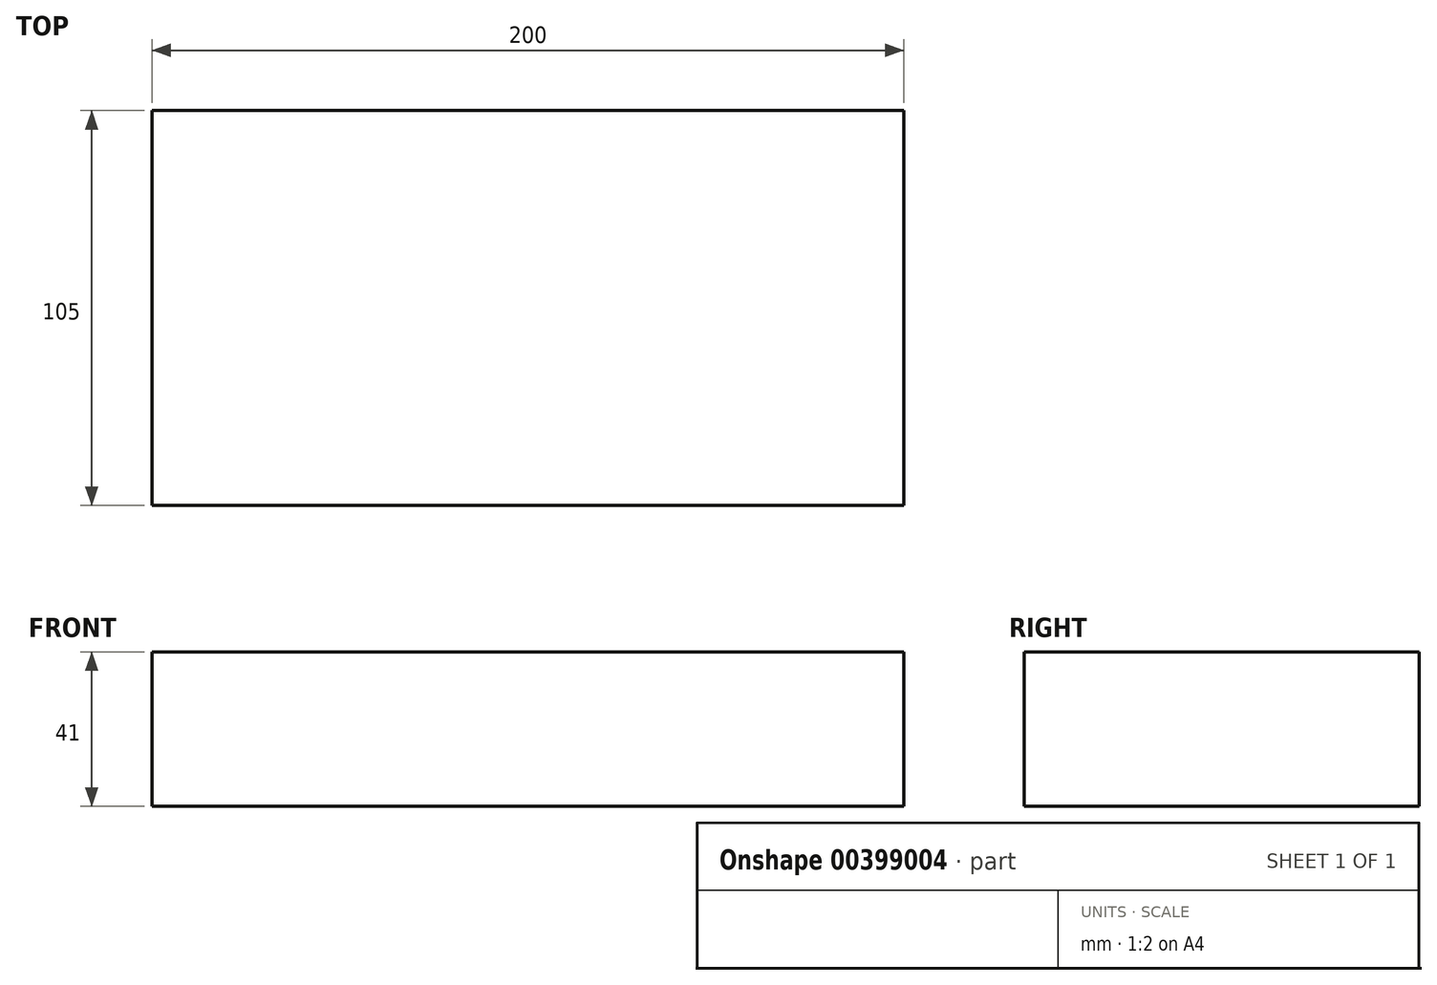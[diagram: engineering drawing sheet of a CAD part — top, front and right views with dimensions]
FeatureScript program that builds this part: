
annotation { "Feature Type Name" : "Feature", "Feature Type Description" : "" }
export const myFeature = defineFeature(function(context is Context, id is Id, definition is map)
    precondition{}
    {
        {
            var Q0;
            Q0=qCreatedBy(makeId("Front.planeOp"),FACE);
            var sketch = newSketch(context, id + "F0", { "sketchPlane" : qUnion([Q0])});
            skLineSegment(sketch, "E0.bottom", {"start": v(0, 0) * mm, "end": v(200, 0) * mm});
            skLineSegment(sketch, "E0.top", {"start": v(0, 41) * mm, "end": v(200, 41) * mm});
            skLineSegment(sketch, "E0.left", {"start": v(0, 0) * mm, "end": v(0, 41) * mm});
            skLineSegment(sketch, "E0.right", {"start": v(200, 0) * mm, "end": v(200, 41) * mm});
            skSolve(sketch);
        }
        {
            var Q0;
            Q0=makeQuery(id+"F0.imprint","IMPRINT",FACE,{"disambiguationData":[TD([[makeQuery(id+"F0.imprint","IMPRINT",EDGE,{"derivedFrom":sQuery(id+"F0.wireOp",EDGE,"E0.bottom")}),1.0]])]});
            extrude(context, id + "F1", {"entities" : qUnion([Q0]), "depth" : 105 * mm});
        }
    });
